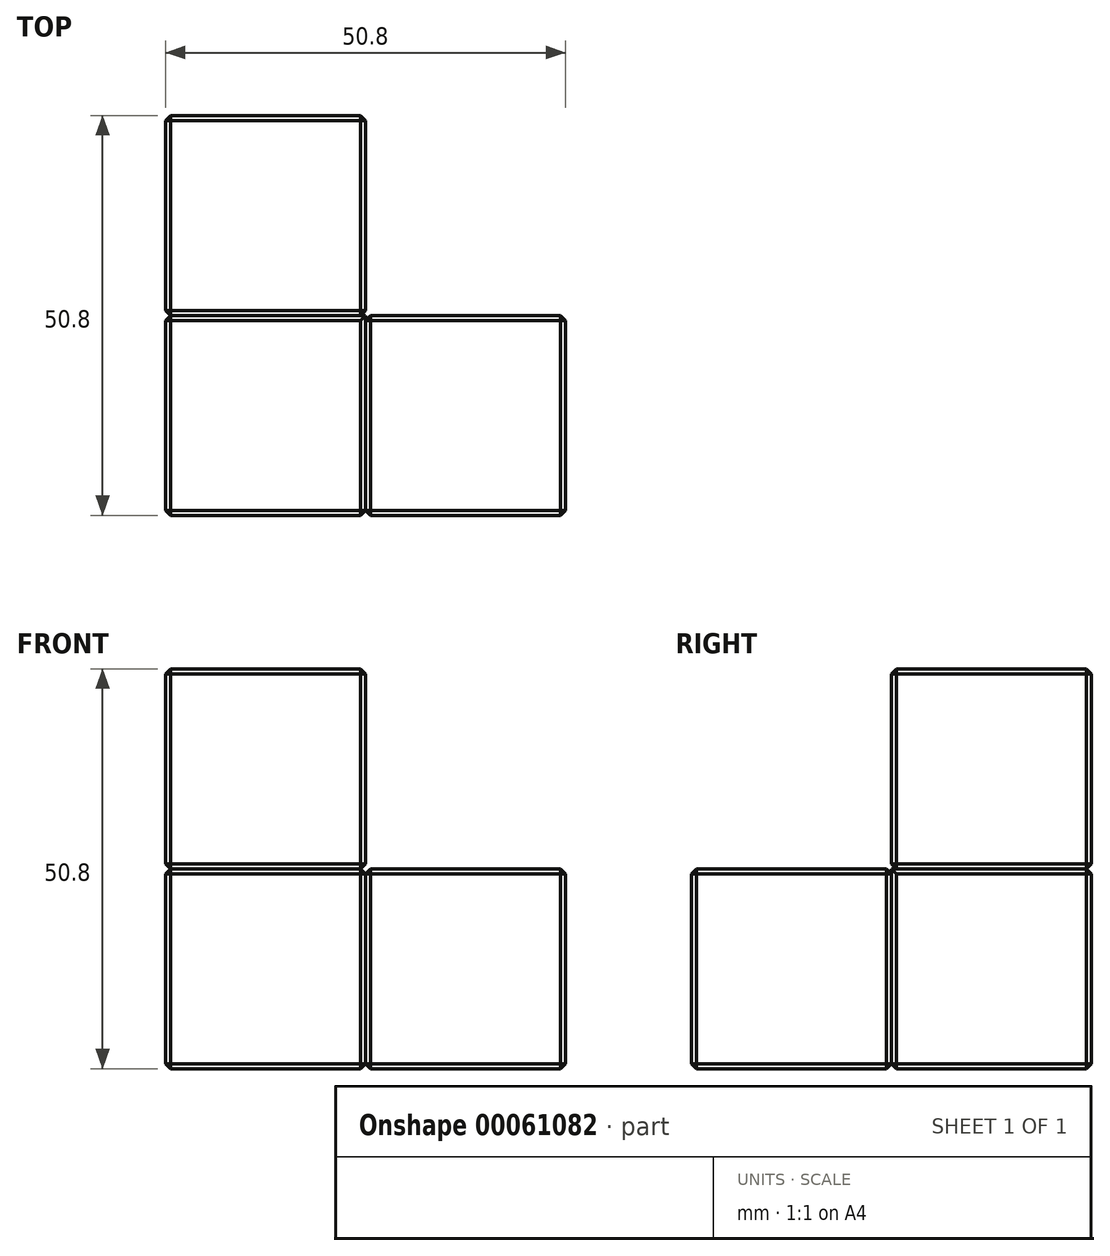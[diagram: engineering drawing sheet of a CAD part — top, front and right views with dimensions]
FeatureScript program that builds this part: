
annotation { "Feature Type Name" : "Feature", "Feature Type Description" : "" }
export const myFeature = defineFeature(function(context is Context, id is Id, definition is map)
    precondition{}
    {
        {
            var Q0;
            Q0=qCreatedBy(makeId("Top.planeOp"),FACE);
            var sketch = newSketch(context, id + "F0", { "sketchPlane" : qUnion([Q0])});
            skLineSegment(sketch, "E0.rect.bottom", {"start": v(-12.7, 12.7) * mm, "end": v(12.7, 12.7) * mm});
            skLineSegment(sketch, "E0.rect.top", {"start": v(-12.7, -12.7) * mm, "end": v(12.7, -12.7) * mm});
            skLineSegment(sketch, "E0.rect.left", {"start": v(-12.7, 12.7) * mm, "end": v(-12.7, -12.7) * mm});
            skLineSegment(sketch, "E0.rect.right", {"start": v(12.7, 12.7) * mm, "end": v(12.7, -12.7) * mm});
            skPoint(sketch, "E0.rect.middle", {"position": v(0, 0) * mm});
            skLineSegment(sketch, "E1.top", {"start": v(-12.7, 38.1) * mm, "end": v(12.7, 38.1) * mm});
            skLineSegment(sketch, "E1.left", {"start": v(-12.7, 12.7) * mm, "end": v(-12.7, 38.1) * mm});
            skLineSegment(sketch, "E1.right", {"start": v(12.7, 12.7) * mm, "end": v(12.7, 38.1) * mm});
            skLineSegment(sketch, "E2.bottom", {"start": v(12.7, 12.7) * mm, "end": v(38.1, 12.7) * mm});
            skLineSegment(sketch, "E2.top", {"start": v(12.7, -12.7) * mm, "end": v(38.1, -12.7) * mm});
            skLineSegment(sketch, "E2.right", {"start": v(38.1, 12.7) * mm, "end": v(38.1, -12.7) * mm});
            skSolve(sketch);
        }
        {
            var Q0;
            Q0=makeQuery(id+"F0.imprint","IMPRINT",FACE,{"disambiguationData":[TD([[makeQuery(id+"F0.imprint","IMPRINT",EDGE,{"derivedFrom":sQuery(id+"F0.wireOp",EDGE,"E0.rect.top")}),1.0]])]});
            extrude(context, id + "F1", {"entities" : qUnion([Q0]), "depth" : 25.4 * mm});
        }
        {
            var Q0;
            Q0=makeQuery(id+"F0.imprint","IMPRINT",FACE,{"disambiguationData":[TD([[makeQuery(id+"F0.imprint","IMPRINT",EDGE,{"derivedFrom":sQuery(id+"F0.wireOp",EDGE,"E2.bottom")}),-1.0]])]});
            var Q1;
            Q1=makeQuery(id+"F0.imprint","IMPRINT",FACE,{"disambiguationData":[TD([[makeQuery(id+"F0.imprint","IMPRINT",EDGE,{"derivedFrom":sQuery(id+"F0.wireOp",EDGE,"E0.rect.bottom")}),1.0]])]});
            extrude(context, id + "F2", {"entities" : qUnion([Q0, Q1]), "depth" : 25.4 * mm});
        }
        {
            var Q0;
            Q0=makeQuery(id+"F2.opExtrude","CAP_FACE",FACE,{"disambiguationData":[OSD([sQuery(id+"F0.wireOp",EDGE,"E0.rect.bottom"),sQuery(id+"F0.wireOp",EDGE,"E1.top"),sQuery(id+"F0.wireOp",EDGE,"E1.left"),sQuery(id+"F0.wireOp",EDGE,"E1.right")])],"isStart":false});
            extrude(context, id + "F3", {"entities" : qUnion([Q0]), "depth" : 25.4 * mm});
        }
        {
            var Q0;
            Q0=makeQuery(id+"F1.opExtrude","CAP_FACE",FACE,{"disambiguationData":[OSD([sQuery(id+"F0.wireOp",EDGE,"E0.rect.top"),sQuery(id+"F0.wireOp",EDGE,"E0.rect.left"),sQuery(id+"F0.wireOp",EDGE,"E0.rect.bottom"),sQuery(id+"F0.wireOp",EDGE,"E0.rect.right")])],"isStart":false});
            var Q1;
            Q1=makeQuery(id+"F1.opExtrude","SWEPT_FACE",FACE,{"disambiguationData":[OSD([sQuery(id+"F0.wireOp",EDGE,"E0.rect.top")])]});
            var Q2;
            Q2=makeQuery(id+"F2.opExtrude","SWEPT_FACE",FACE,{"disambiguationData":[OSD([sQuery(id+"F0.wireOp",EDGE,"E2.top")])]});
            var Q3;
            Q3=makeQuery(id+"F2.opExtrude","CAP_FACE",FACE,{"disambiguationData":[OSD([sQuery(id+"F0.wireOp",EDGE,"E2.bottom"),sQuery(id+"F0.wireOp",EDGE,"E2.top"),sQuery(id+"F0.wireOp",EDGE,"E0.rect.right"),sQuery(id+"F0.wireOp",EDGE,"E2.right")])],"isStart":false});
            var Q4;
            Q4=makeQuery(id+"F3.opExtrude","SWEPT_FACE",FACE,{"disambiguationData":[OSD([sQuery(id+"F0.wireOp",EDGE,"E0.rect.bottom")])]});
            var Q5;
            Q5=makeQuery(id+"F3.opExtrude","SWEPT_FACE",FACE,{"disambiguationData":[OSD([sQuery(id+"F0.wireOp",EDGE,"E1.right")])]});
            var Q6;
            Q6=makeQuery(id+"F3.opExtrude","CAP_FACE",FACE,{"disambiguationData":[OSD([sQuery(id+"F0.wireOp",EDGE,"E0.rect.bottom"),sQuery(id+"F0.wireOp",EDGE,"E1.top"),sQuery(id+"F0.wireOp",EDGE,"E1.left"),sQuery(id+"F0.wireOp",EDGE,"E1.right")])],"isStart":false});
            var Q7;
            Q7=makeQuery(id+"F2.opExtrude","SWEPT_FACE",FACE,{"disambiguationData":[OSD([sQuery(id+"F0.wireOp",EDGE,"E2.bottom")])]});
            var Q8;
            Q8=makeQuery(id+"F2.opExtrude","SWEPT_FACE",FACE,{"disambiguationData":[OSD([sQuery(id+"F0.wireOp",EDGE,"E1.top")])]});
            var Q9;
            Q9=makeQuery(id+"F2.opExtrude","SWEPT_FACE",FACE,{"disambiguationData":[OSD([sQuery(id+"F0.wireOp",EDGE,"E1.left")])]});
            var Q10;
            Q10=makeQuery(id+"F3.opExtrude","SWEPT_FACE",FACE,{"disambiguationData":[OSD([sQuery(id+"F0.wireOp",EDGE,"E1.left")])]});
            var Q11;
            Q11=makeQuery(id+"F1.opExtrude","SWEPT_FACE",FACE,{"disambiguationData":[OSD([sQuery(id+"F0.wireOp",EDGE,"E0.rect.left")])]});
            var Q12;
            Q12=makeQuery(id+"F1.opExtrude","CAP_FACE",FACE,{"disambiguationData":[OSD([sQuery(id+"F0.wireOp",EDGE,"E0.rect.top"),sQuery(id+"F0.wireOp",EDGE,"E0.rect.left"),sQuery(id+"F0.wireOp",EDGE,"E0.rect.bottom"),sQuery(id+"F0.wireOp",EDGE,"E0.rect.right")])],"isStart":true});
            var Q13;
            Q13=makeQuery(id+"F2.opExtrude","CAP_FACE",FACE,{"disambiguationData":[OSD([sQuery(id+"F0.wireOp",EDGE,"E2.bottom"),sQuery(id+"F0.wireOp",EDGE,"E2.top"),sQuery(id+"F0.wireOp",EDGE,"E0.rect.right"),sQuery(id+"F0.wireOp",EDGE,"E2.right")])],"isStart":true});
            var Q14;
            Q14=makeQuery(id+"F2.opExtrude","CAP_FACE",FACE,{"disambiguationData":[OSD([sQuery(id+"F0.wireOp",EDGE,"E0.rect.bottom"),sQuery(id+"F0.wireOp",EDGE,"E1.top"),sQuery(id+"F0.wireOp",EDGE,"E1.left"),sQuery(id+"F0.wireOp",EDGE,"E1.right")])],"isStart":true});
            var Q15;
            Q15=makeQuery(id+"F2.opExtrude","SWEPT_FACE",FACE,{"disambiguationData":[OSD([sQuery(id+"F0.wireOp",EDGE,"E1.right")])]});
            var Q16;
            Q16=makeQuery(id+"F3.opExtrude","SWEPT_FACE",FACE,{"disambiguationData":[OSD([sQuery(id+"F0.wireOp",EDGE,"E1.top")])]});
            chamfer(context, id + "F4", {"entities" : qUnion([Q0, Q1, Q2, Q3, Q4, Q5, Q6, Q7, Q8, Q9, Q10, Q11, Q12, Q13, Q14, Q15, Q16]), "width" : 0.64 * mm, "tangentPropagation" : true});
        }
    });
